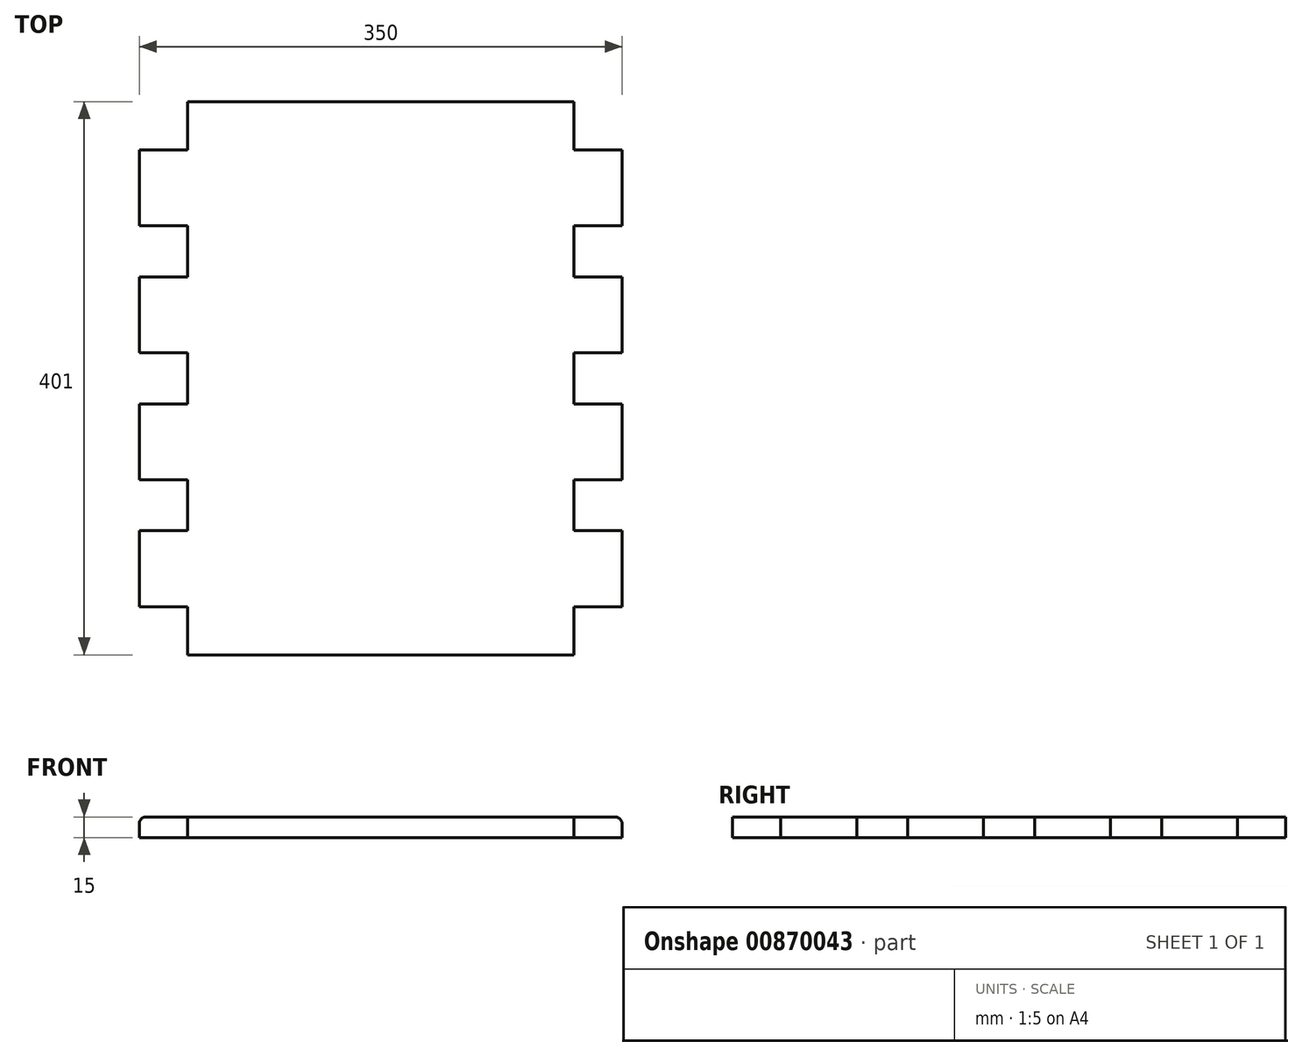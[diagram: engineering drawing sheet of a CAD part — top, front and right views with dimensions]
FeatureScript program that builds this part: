
annotation { "Feature Type Name" : "Feature", "Feature Type Description" : "" }
export const myFeature = defineFeature(function(context is Context, id is Id, definition is map)
    precondition{}
    {
        {
            var Q0;
            Q0=qCreatedBy(makeId("Top.planeOp"),FACE);
            var sketch = newSketch(context, id + "F0", { "sketchPlane" : qUnion([Q0])});
            skLineSegment(sketch, "E0", {"start": v(-175, 165.5) * mm, "end": v(-175, 110.5) * mm});
            skLineSegment(sketch, "E1", {"start": v(-175, 110.5) * mm, "end": v(-140, 110.5) * mm});
            skLineSegment(sketch, "E2", {"start": v(-140, 110.5) * mm, "end": v(-140, 73.5) * mm});
            skLineSegment(sketch, "E3", {"start": v(-140, 73.5) * mm, "end": v(-175, 73.5) * mm});
            skLineSegment(sketch, "E4", {"start": v(-175, 73.5) * mm, "end": v(-175, 18.5) * mm});
            skLineSegment(sketch, "E5", {"start": v(-175, 18.5) * mm, "end": v(-140, 18.5) * mm});
            skLineSegment(sketch, "E6", {"start": v(-140, 18.5) * mm, "end": v(-140, 0) * mm});
            skLineSegment(sketch, "E7", {"start": v(-140, 0) * mm, "end": v(0, 0) * mm});
            skLineSegment(sketch, "E8", {"start": v(0, 200.5) * mm, "end": v(-140, 200.5) * mm});
            skLineSegment(sketch, "E9", {"start": v(-140, 200.5) * mm, "end": v(-140, 165.5) * mm});
            skLineSegment(sketch, "E10", {"start": v(-175, 165.5) * mm, "end": v(-140, 165.5) * mm});
            skLineSegment(sketch, "E11", {"start": v(-140, 165.5) * mm, "end": v(-140, 110.5) * mm, "construction": true});
            skLineSegment(sketch, "E12", {"start": v(-140, 73.5) * mm, "end": v(-140, 18.5) * mm, "construction": true});
            skLineSegment(sketch, "E13", {"start": v(-175, 18.5) * mm, "end": v(-175, 0) * mm, "construction": true});
            skLineSegment(sketch, "E14", {"start": v(-175, 110.5) * mm, "end": v(-175, 73.5) * mm, "construction": true});
            skPoint(sketch, "E15", {"position": v(-175, 92) * mm});
            skLineSegment(sketch, "E16", {"start": v(-175, 92) * mm, "end": v(-175, 73.5) * mm, "construction": true});
            skLineSegment(sketch, "E17", {"start": v(0, 0) * mm, "end": v(0, 0) * mm});
            skLineSegment(sketch, "E18", {"start": v(0, 0) * mm, "end": v(0, 200.5) * mm});
            skSolve(sketch);
        }
        {
            var Q0;
            Q0 = qSketchRegion(id + "F0", true);
            extrude(context, id + "F1", {"entities" : qUnion([Q0]), "depth" : 15 * mm, "offsetDistance" : 25 * mm});
        }
        {
            var Q0;
            Q0=makeQuery(id+"F1.opExtrude","SWEPT_BODY",BODY,{"disambiguationData":[OSD([sQuery(id+"F0.wireOp",EDGE,"E0"),sQuery(id+"F0.wireOp",EDGE,"E1"),sQuery(id+"F0.wireOp",EDGE,"E2"),sQuery(id+"F0.wireOp",EDGE,"E3"),sQuery(id+"F0.wireOp",EDGE,"E4"),sQuery(id+"F0.wireOp",EDGE,"E5"),sQuery(id+"F0.wireOp",EDGE,"E6"),sQuery(id+"F0.wireOp",EDGE,"E7"),sQuery(id+"F0.wireOp",EDGE,"aX8AaR7b-QMlM-42ii-P0kL-P2bNqVa3d87b"),sQuery(id+"F0.wireOp",EDGE,"E8"),sQuery(id+"F0.wireOp",EDGE,"E9"),sQuery(id+"F0.wireOp",EDGE,"E10")])]});
            var Q1;
            Q1=qCreatedBy(makeId("Front.planeOp"),FACE);
            mirror(context, id + "F2", {"operationType" : NewBodyOperationType.ADD, "entities" : qUnion([Q0]), "mirrorPlane" : qUnion([Q1])});
        }
        {
            var Q0;
            Q0=makeQuery(id+"F1.opExtrude","CAP_EDGE",EDGE,{"disambiguationData":[OSD([sQuery(id+"F0.wireOp",EDGE,"E0")])],"isStart":false});
            var Q1;
            Q1=makeQuery(id+"F1.opExtrude","CAP_EDGE",EDGE,{"disambiguationData":[OSD([sQuery(id+"F0.wireOp",EDGE,"E4")])],"isStart":false});
            var Q2;
            Q2=makeQuery(id+"F2.opPattern","COPY",EDGE,{"derivedFrom":makeQuery(id+"F1.opExtrude","CAP_EDGE",EDGE,{"disambiguationData":[OSD([sQuery(id+"F0.wireOp",EDGE,"E4")])],"isStart":false}),"instanceName":"1"});
            var Q3;
            Q3=makeQuery(id+"F2.opPattern","COPY",EDGE,{"derivedFrom":makeQuery(id+"F1.opExtrude","CAP_EDGE",EDGE,{"disambiguationData":[OSD([sQuery(id+"F0.wireOp",EDGE,"E0")])],"isStart":false}),"instanceName":"1"});
            fillet(context, id + "F3", {"entities" : qUnion([Q0, Q1, Q2, Q3]), "radius" : 5 * mm, "tangentPropagation" : true, "allowEdgeOverflow" : false});
        }
        {
            var Q0;
            Q0=makeQuery(id+"F1.opExtrude","SWEPT_BODY",BODY,{"disambiguationData":[OSD([sQuery(id+"F0.wireOp",EDGE,"E0"),sQuery(id+"F0.wireOp",EDGE,"E1"),sQuery(id+"F0.wireOp",EDGE,"E2"),sQuery(id+"F0.wireOp",EDGE,"E3"),sQuery(id+"F0.wireOp",EDGE,"E4"),sQuery(id+"F0.wireOp",EDGE,"E5"),sQuery(id+"F0.wireOp",EDGE,"E6"),sQuery(id+"F0.wireOp",EDGE,"E7"),sQuery(id+"F0.wireOp",EDGE,"E8"),sQuery(id+"F0.wireOp",EDGE,"E9"),sQuery(id+"F0.wireOp",EDGE,"E10"),sQuery(id+"F0.wireOp",EDGE,"E18")])]});
            var Q1;
            {var subQ0=makeQuery(id+"F1.opExtrude","SWEPT_FACE",FACE,{"disambiguationData":[OSD([sQuery(id+"F0.wireOp",EDGE,"E18")])]});Q1=makeQuery(id+"F2.boolean.opBoolean","MERGE",FACE,{"derivedFrom":[subQ0,makeQuery(id+"F2.opPattern","COPY",FACE,{"derivedFrom":subQ0,"instanceName":"1"})]});}
            mirror(context, id + "F4", {"operationType" : NewBodyOperationType.ADD, "entities" : qUnion([Q0]), "mirrorPlane" : qUnion([Q1])});
        }
    });
